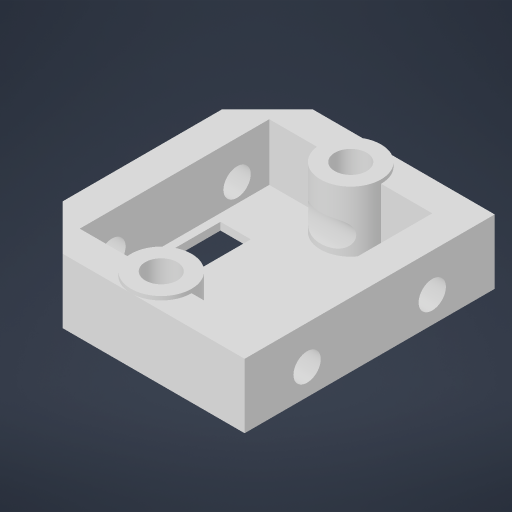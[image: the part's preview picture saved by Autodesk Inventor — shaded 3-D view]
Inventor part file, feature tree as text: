
AUTODESK INVENTOR PART (.ipt)
format: ipt  version: 2024.1 (Build 281209000, 209)  size: 294,400 bytes
history: native  units: mm
features: extrude x8, sketch x6, plane x2, projected_geometry x2, chamfer x1
ambient origin geometry x8: Origin, YZ Plane, XZ Plane, XY Plane, X Axis, Y Axis, Z Axis, Center Point
bodies: Solid1 (feature_tree)
feature tree (19):
  extrude  "Extrusion1"  Depth=20.0mm
  extrude  "Extrusion2"  Depth=25.0mm
  extrude  "Extrusion3"  Depth=4.0mm
  sketch  "Sketch4"  dims[d7=6.5mm d9=10.0mm]
  extrude  "Extrusion5"  Depth=10.0mm
  sketch  "Sketch6"  dims[d12=1.0mm d13=0.0mm d14=8.0mm d15=0.0mm]
  plane  "Work Plane1"
  extrude  "Extrusion6"  Depth=8.0mm TaperAngle=0.0deg
  plane  "Work Plane2"
  extrude  "Extrusion7"  Depth=10.0mm
  extrude  "Extrusion8"  Depth=10.0mm
  extrude  "Extrusion9"  Depth=10.0mm TaperAngle=0.0deg
  chamfer  "Chamfer1"  Distance=3.6mm
  sketch  "Sketch1"  dims[d0=15.0mm d1=20.0mm]
  sketch  "Sketch2"  dims[d2=4.2mm d3=25.0mm]
  projected_geometry  "Projected Loop1"
  sketch  "Sketch3"  dims[d4=5.0mm d6=4.0mm]
  projected_geometry  "Projected Loop2"
  sketch  "Sketch8"  dims[d16=4.0mm d17=2.5mm d18=1.0mm d21=7.5mm d22=0.0mm d23=3.6mm d24=16.51mm d28=10.0mm d29=0.0mm d31=2.25mm d32=0.0mm d33=5.25mm d34=0.0mm d35=10.0mm d36=0.0mm d37=33.5mm d38=0.0mm d39=6.0mm d40=2.0mm d41=45.0deg d26=0.5mm d27=0.872665mm]
